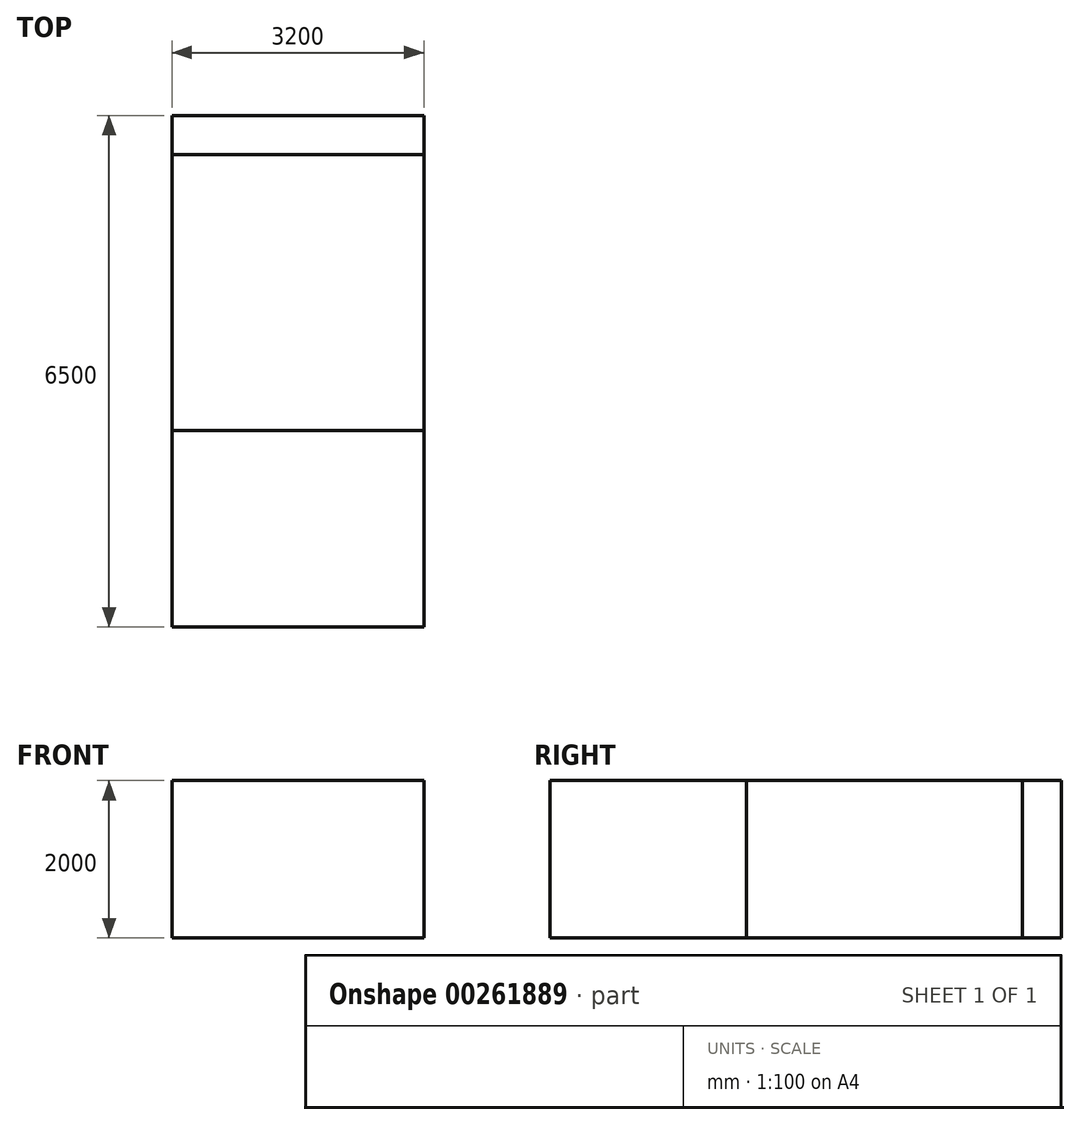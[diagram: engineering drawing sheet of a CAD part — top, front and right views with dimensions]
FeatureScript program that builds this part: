
annotation { "Feature Type Name" : "Feature", "Feature Type Description" : "" }
export const myFeature = defineFeature(function(context is Context, id is Id, definition is map)
    precondition{}
    {
        {
            var Q0;
            Q0=qCreatedBy(makeId("Front.planeOp"),FACE);
            var sketch = newSketch(context, id + "F0", { "sketchPlane" : qUnion([Q0])});
            skLineSegment(sketch, "E0.bottom", {"start": v(-1600, 1000) * mm, "end": v(1600, 1000) * mm});
            skLineSegment(sketch, "E0.top", {"start": v(-1600, -1000) * mm, "end": v(1600, -1000) * mm});
            skLineSegment(sketch, "E0.left", {"start": v(-1600, 1000) * mm, "end": v(-1600, -1000) * mm});
            skLineSegment(sketch, "E0.right", {"start": v(1600, 1000) * mm, "end": v(1600, -1000) * mm});
            skPoint(sketch, "E0.middle", {"position": v(0, 0) * mm});
            skSolve(sketch);
        }
        {
            var Q0;
            Q0=makeQuery(id+"F0.imprint","IMPRINT",FACE,{"disambiguationData":[TD([[makeQuery(id+"F0.imprint","IMPRINT",EDGE,{"derivedFrom":sQuery(id+"F0.wireOp",EDGE,"E0.bottom")}),-1.0]])]});
            extrude(context, id + "F1", {"entities" : qUnion([Q0]), "depth" : 2500 * mm});
        }
        {
            var Q0;
            Q0=makeQuery(id+"F0.imprint","IMPRINT",FACE,{"disambiguationData":[TD([[makeQuery(id+"F0.imprint","IMPRINT",EDGE,{"derivedFrom":sQuery(id+"F0.wireOp",EDGE,"E0.bottom")}),-1.0]])]});
            extrude(context, id + "F2", {"entities" : qUnion([Q0]), "oppositeDirection" : true, "depth" : 3500 * mm});
        }
        {
            var Q0;
            Q0=makeQuery(id+"F0.imprint","IMPRINT",FACE,{"disambiguationData":[TD([[makeQuery(id+"F0.imprint","IMPRINT",EDGE,{"derivedFrom":sQuery(id+"F0.wireOp",EDGE,"E0.bottom")}),-1.0]])]});
            extrude(context, id + "F3", {"entities" : qUnion([Q0]), "oppositeDirection" : true, "depth" : 4000 * mm});
        }
    });
